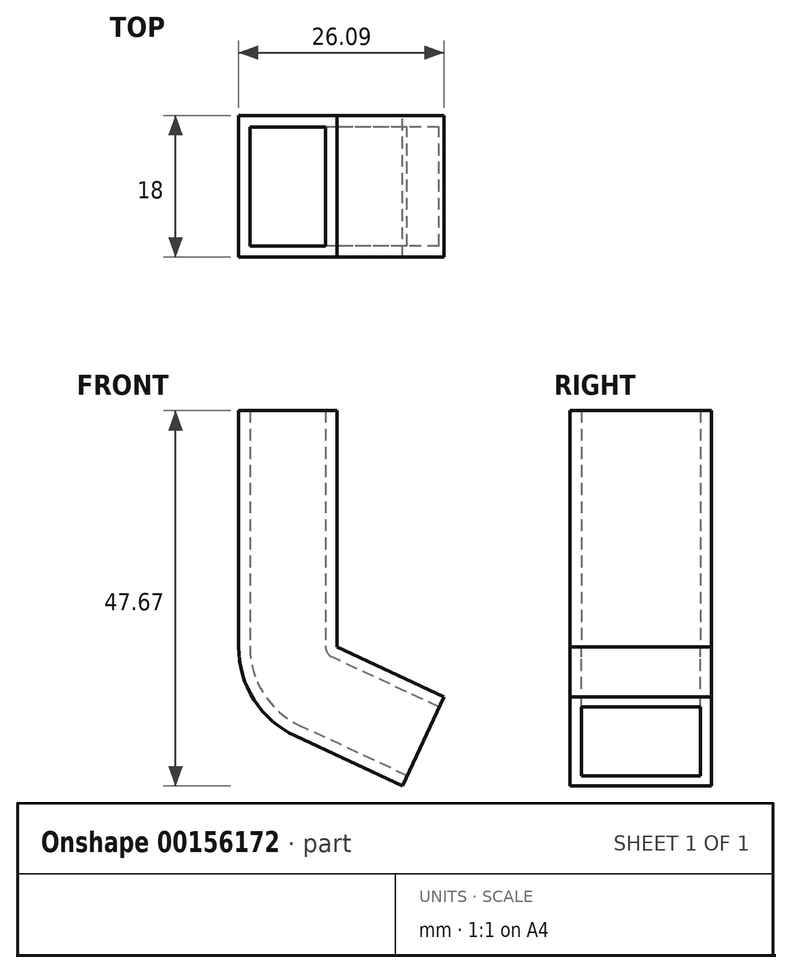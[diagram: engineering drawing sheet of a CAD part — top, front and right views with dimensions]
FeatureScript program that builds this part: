
annotation { "Feature Type Name" : "Feature", "Feature Type Description" : "" }
export const myFeature = defineFeature(function(context is Context, id is Id, definition is map)
    precondition{}
    {
        {
            var Q0;
            Q0=qCreatedBy(makeId("Top.planeOp"),FACE);
            var sketch = newSketch(context, id + "F0", { "sketchPlane" : qUnion([Q0])});
            skLineSegment(sketch, "E0.bottom", {"start": v(6.25, -9) * mm, "end": v(-6.25, -9) * mm});
            skLineSegment(sketch, "E0.top", {"start": v(6.25, 9) * mm, "end": v(6.25, 9) * mm});
            skLineSegment(sketch, "E0.left", {"start": v(6.25, -9) * mm, "end": v(6.25, -9) * mm});
            skLineSegment(sketch, "E0.right", {"start": v(-6.25, -9) * mm, "end": v(-6.25, -9) * mm});
            skPoint(sketch, "E0.middle", {"position": v(0, 0) * mm});
            skLineSegment(sketch, "E1.0", {"start": v(4.81, 7.56) * mm, "end": v(4.81, 7.56) * mm});
            skLineSegment(sketch, "E1.1", {"start": v(4.81, -7.56) * mm, "end": v(4.81, -7.56) * mm});
            skLineSegment(sketch, "E1.2", {"start": v(4.81, -7.56) * mm, "end": v(-4.8, -7.56) * mm});
            skLineSegment(sketch, "E1.3", {"start": v(-4.8, -7.56) * mm, "end": v(-4.8, 7.56) * mm});
            skLineSegment(sketch, "E2", {"start": v(6.25, 9) * mm, "end": v(-6.25, 9) * mm});
            skLineSegment(sketch, "E3", {"start": v(6.25, -9) * mm, "end": v(6.25, 9) * mm});
            skLineSegment(sketch, "E4", {"start": v(-6.25, -9) * mm, "end": v(-6.25, 9) * mm});
            skLineSegment(sketch, "E5", {"start": v(-6.25, 9) * mm, "end": v(-6.25, 9) * mm});
            skLineSegment(sketch, "E6", {"start": v(-4.8, 7.56) * mm, "end": v(-4.8, 7.56) * mm});
            skLineSegment(sketch, "E7", {"start": v(4.81, 7.56) * mm, "end": v(-4.8, 7.56) * mm});
            skLineSegment(sketch, "E8", {"start": v(4.81, -7.56) * mm, "end": v(4.81, 7.56) * mm});
            skLineSegment(sketch, "E9", {"start": v(-4.8, -7.56) * mm, "end": v(-4.8, -7.56) * mm});
            skSolve(sketch);
        }
        {
            var Q0;
            Q0 = qSketchRegion(id + "F0", true);
            extrude(context, id + "F1", {"entities" : qUnion([Q0]), "depth" : 30 * mm});
        }
        {
            var Q0;
            Q0=makeQuery(id+"F1.opExtrude","CAP_FACE",FACE,{"disambiguationData":[OSD([sQuery(id+"F0.wireOp",EDGE,"E0.bottom"),sQuery(id+"F0.wireOp",EDGE,"E1.2"),sQuery(id+"F0.wireOp",EDGE,"E1.3"),sQuery(id+"F0.wireOp",EDGE,"E2"),sQuery(id+"F0.wireOp",EDGE,"E3"),sQuery(id+"F0.wireOp",EDGE,"E4"),sQuery(id+"F0.wireOp",EDGE,"E7"),sQuery(id+"F0.wireOp",EDGE,"E8")])],"isStart":true});
            var Q1;
            Q1=makeQuery(id+"F1.opExtrude","CAP_EDGE",EDGE,{"disambiguationData":[OSD([sQuery(id+"F0.wireOp",EDGE,"E3")])],"isStart":true});
            revolve(context, id + "F2", {"operationType" : NewBodyOperationType.ADD, "entities" : qUnion([Q0]), "axis" : qUnion([Q1]), "revolveType" : RevolveType.ONE_DIRECTION, "oppositeDirection" : true, "angle" : 65 * degree});
        }
        {
            var Q0;
            Q0=makeQuery(id+"F2.opRevolve","CAP_FACE",FACE,{"disambiguationData":[OSD([sQuery(id+"F0.wireOp",EDGE,"E0.bottom"),sQuery(id+"F0.wireOp",EDGE,"E1.2"),sQuery(id+"F0.wireOp",EDGE,"E1.3"),sQuery(id+"F0.wireOp",EDGE,"E2"),sQuery(id+"F0.wireOp",EDGE,"E3"),sQuery(id+"F0.wireOp",EDGE,"E4"),sQuery(id+"F0.wireOp",EDGE,"E7"),sQuery(id+"F0.wireOp",EDGE,"E8")])],"isStart":false});
            extrude(context, id + "F3", {"entities" : qUnion([Q0]), "operationType" : NewBodyOperationType.ADD, "depth" : 15 * mm});
        }
    });
